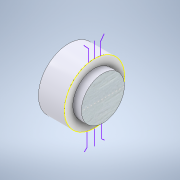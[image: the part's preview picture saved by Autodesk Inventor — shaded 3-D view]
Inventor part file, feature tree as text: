
AUTODESK INVENTOR PART (.ipt)
format: ipt  version: 2021 (Build 250183000, 183)  size: 134,144 bytes
history: native  units: mm
features: sketch x7, extrude x2
ambient origin geometry x8: Origin, YZ Plane, XZ Plane, XY Plane, X Axis, Y Axis, Z Axis, Center Point
bodies: Solid1 (feature_tree)
feature tree (9):
  extrude  "Extrusion1"  Depth=15.0mm TaperAngle=0.0deg
  extrude  "Extrusion2"  Depth=5.0mm TaperAngle=0.0deg
  sketch  "Sketch3"  dims[d6=9.0mm]
  sketch  "Sketch4"  dims[d7=9.0mm]
  sketch  "Sketch5"
  sketch  "Sketch6"
  sketch  "Sketch7"
  sketch  "Sketch1"  dims[d0=35.0mm d1=15.0mm d2=0.0mm]
  sketch  "Sketch2"  dims[d3=25.0mm d4=5.0mm d5=0.0mm]
